# Revit family: SUPERBRILLOSA DIFUSA 2216_S242300W.1
name_source: partatom
category: Luminarias
units: mm (PartAtom-declared; Revit-internal decimal feet)

## family parameters
Compartido = No
Corte con vacíos al cargar = No
Cota de conector redondo = Diámetro de uso
Origen de luz = Sí
Punto de cálculo de habitación = No
Se basa en plano de trabajo = Sí
Siempre vertical = No
Tipo de pieza = Normal

## types (1)
- SUPERBRILLOSA DIFUSA 2216_S242300W.1
    Archivo de red fotométrica = S242300W.1.IES
    Cambio de temperatura de color de luz atenuada = <Ninguno>
    Comentarios de vataje = 24
    Descripción = TIRA LUMINOSA MONOCROMATICADE PCB BLANCO CON RECUBRIMIENTO DE PLASTICO CON UNA POTENCIA DE 15W/M, USO PARA EXTERIORES IP66, IRC 90,  TEMPERATURA EN BLANCO CALIDO 3000K, 1275 LUMENES/M, PRESENTACION DE 5M, CORTE 2.5CM, ALIMENTADO A 24V, REQUIERE ACCESORIOS.
    Elevación por defecto = 0 mm  [stored 0 ft]
    Fabricante = BRILLANT
    Filtro de color = 16777215
    Longitud de línea de emisión = 600 mm
    Marca = BRILLANT
    Modelo = S242300W.1
    Ángulo de inclinación = 60.00°

note: [stored X ft] marks values corroborated as IEEE doubles in the binary element streams (Revit-internal decimal feet)

## geometry (parser evidence)
native form markers: Blend x2
no freeform markers — native parametric forms only
